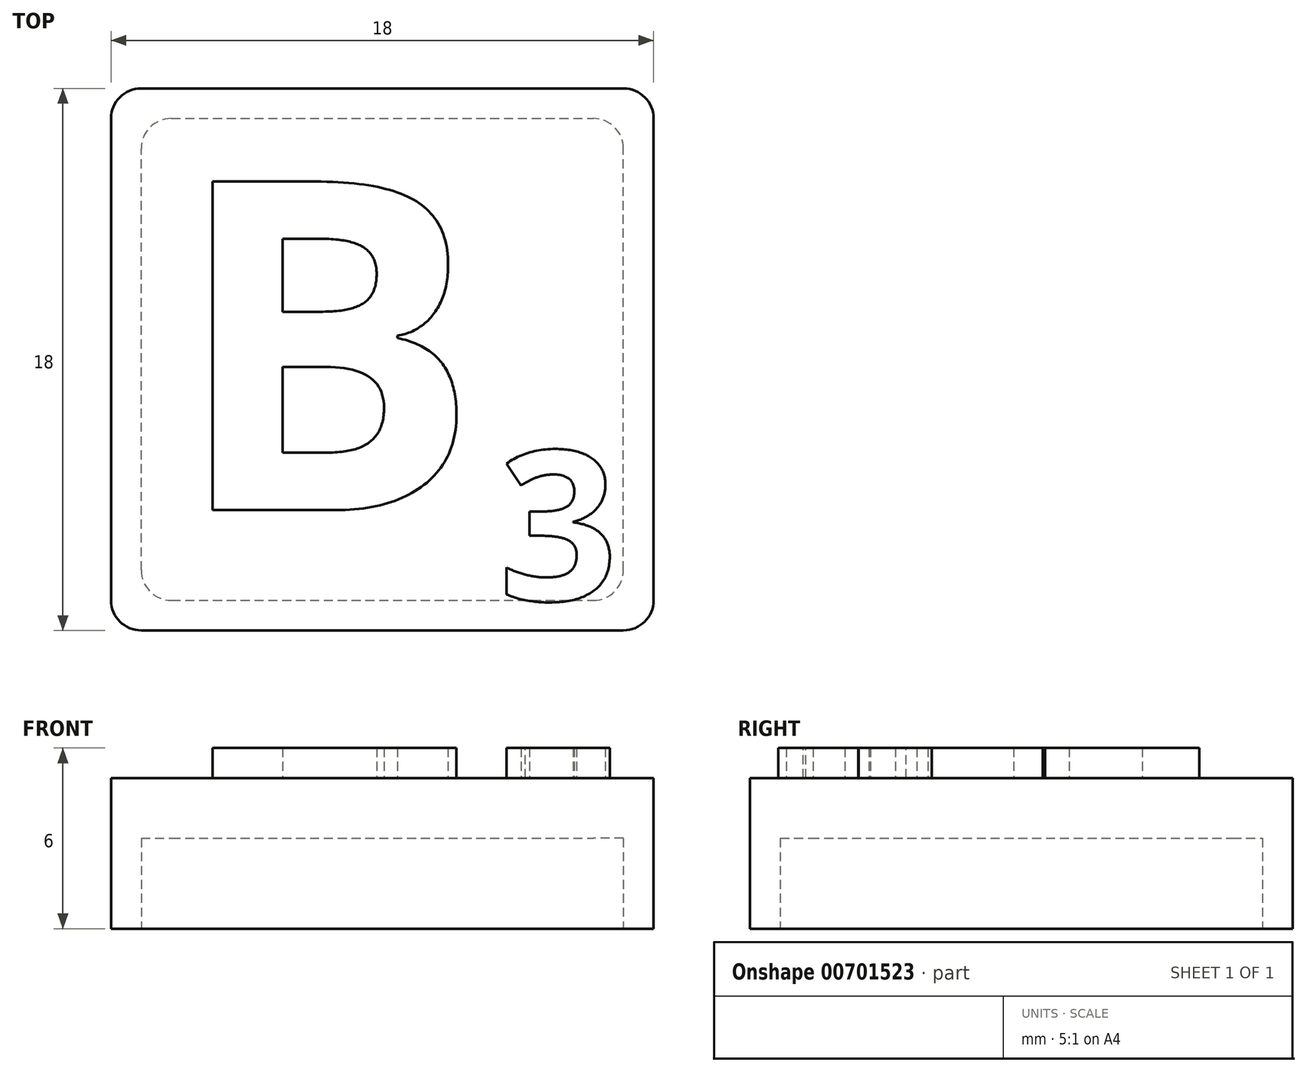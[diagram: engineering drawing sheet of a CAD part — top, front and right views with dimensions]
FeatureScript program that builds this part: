
annotation { "Feature Type Name" : "Feature", "Feature Type Description" : "" }
export const myFeature = defineFeature(function(context is Context, id is Id, definition is map)
    precondition{}
    {
        {
            var Q0;
            Q0=qCreatedBy(makeId("Top.planeOp"),FACE);
            var sketch = newSketch(context, id + "F0", { "sketchPlane" : qUnion([Q0])});
            skLineSegment(sketch, "E0.bottom", {"start": v(-3.93, 7.24) * mm, "end": v(14.07, 7.24) * mm});
            skLineSegment(sketch, "E0.top", {"start": v(-3.93, -10.76) * mm, "end": v(14.07, -10.76) * mm});
            skLineSegment(sketch, "E0.left", {"start": v(-3.93, 7.24) * mm, "end": v(-3.93, -10.76) * mm});
            skLineSegment(sketch, "E0.right", {"start": v(14.07, 7.24) * mm, "end": v(14.07, -10.76) * mm});
            skSolve(sketch);
        }
        {
            var Q0;
            Q0=qSketchRegion(id+"F0",true);
            extrude(context, id + "F1", {"entities" : qUnion([Q0]), "depth" : 5 * mm, "offsetDistance" : 25 * mm});
        }
        {
            var Q0;
            Q0=qCreatedBy(makeId("Top.planeOp"),FACE);
            var sketch = newSketch(context, id + "F2", { "sketchPlane" : qUnion([Q0])});
            skLineSegment(sketch, "E1.bottom", {"start": v(-2.93, -9.76) * mm, "end": v(13.07, -9.76) * mm});
            skLineSegment(sketch, "E1.top", {"start": v(-2.93, 6.24) * mm, "end": v(13.07, 6.24) * mm});
            skLineSegment(sketch, "E1.left", {"start": v(-2.93, -9.76) * mm, "end": v(-2.93, 6.24) * mm});
            skLineSegment(sketch, "E1.right", {"start": v(13.07, -9.76) * mm, "end": v(13.07, 6.24) * mm});
            skSolve(sketch);
        }
        {
            var Q0;
            Q0=makeQuery(id+"F2.imprint","IMPRINT",FACE,{"disambiguationData":[TD([[makeQuery(id+"F2.imprint","IMPRINT",EDGE,{"derivedFrom":sQuery(id+"F2.wireOp",EDGE,"E1.bottom")}),1.0]])]});
            extrude(context, id + "F3", {"entities" : qUnion([Q0]), "operationType" : NewBodyOperationType.REMOVE, "depth" : 3 * mm, "offsetDistance" : 25 * mm});
        }
        {
            var Q0;
            Q0=makeQuery(id+"F1.opExtrude","CAP_FACE",FACE,{"disambiguationData":[OSD([sQuery(id+"F0.wireOp",EDGE,"E0.bottom"),sQuery(id+"F0.wireOp",EDGE,"E0.top"),sQuery(id+"F0.wireOp",EDGE,"E0.left"),sQuery(id+"F0.wireOp",EDGE,"E0.right")])],"isStart":false});
            var sketch = newSketch(context, id + "F4", { "sketchPlane" : qUnion([Q0])});
            skText(sketch, "E2", { "text": "B", "fontName": "OpenSans-Bold.ttf"});
            skText(sketch, "E3", { "text": "3", "fontName": "OpenSans-Bold.ttf"});
            const initialGuessF4  = {"E2": [-0.00193, -0.00676, 1, 0, 0.011], "E3": [0.00892, -0.00976, 1, 0, 0.005]};
            skSetInitialGuess(sketch, initialGuessF4);
            skSolve(sketch);
        }
        {
            var Q0;
            Q0=makeQuery(id+"F4.imprint","IMPRINT",FACE,{"disambiguationData":[TD([[makeQuery(id+"F4.imprint","IMPRINT",EDGE,{"derivedFrom":sQuery(id+"F4.wireOp",EDGE,"E2.sketch_text.stroke-0")}),-1.0]])]});
            var Q1;
            Q1=makeQuery(id+"F4.imprint","IMPRINT",FACE,{"disambiguationData":[TD([[makeQuery(id+"F4.imprint","IMPRINT",EDGE,{"derivedFrom":sQuery(id+"F4.wireOp",EDGE,"E3.sketch_text.stroke-0")}),-1.0]])]});
            extrude(context, id + "F5", {"entities" : qUnion([Q0, Q1]), "operationType" : NewBodyOperationType.ADD, "depth" : 1 * mm, "offsetDistance" : 25 * mm});
        }
        {
            var Q0;
            Q0=makeQuery(id+"F1.opExtrude","SWEPT_EDGE",EDGE,{"disambiguationData":[OSD([sQuery(id+"F0.wireOp",EDGE,"E0.bottom"),sQuery(id+"F0.wireOp",EDGE,"E0.right")])]});
            var Q1;
            Q1=makeQuery(id+"F1.opExtrude","SWEPT_EDGE",EDGE,{"disambiguationData":[OSD([sQuery(id+"F0.wireOp",EDGE,"E0.top"),sQuery(id+"F0.wireOp",EDGE,"E0.right")])]});
            var Q2;
            Q2=makeQuery(id+"F1.opExtrude","SWEPT_EDGE",EDGE,{"disambiguationData":[OSD([sQuery(id+"F0.wireOp",EDGE,"E0.top"),sQuery(id+"F0.wireOp",EDGE,"E0.left")])]});
            var Q3;
            Q3=makeQuery(id+"F1.opExtrude","SWEPT_EDGE",EDGE,{"disambiguationData":[OSD([sQuery(id+"F0.wireOp",EDGE,"E0.bottom"),sQuery(id+"F0.wireOp",EDGE,"E0.left")])]});
            var Q4;
            Q4=makeQuery(id+"F3.boolean.opBoolean","COPY",EDGE,{"derivedFrom":makeQuery(id+"F3.opExtrude","SWEPT_EDGE",EDGE,{"disambiguationData":[OSD([sQuery(id+"F2.wireOp",EDGE,"E1.bottom"),sQuery(id+"F2.wireOp",EDGE,"E1.right")])]})});
            var Q5;
            Q5=makeQuery(id+"F3.boolean.opBoolean","COPY",EDGE,{"derivedFrom":makeQuery(id+"F3.opExtrude","SWEPT_EDGE",EDGE,{"disambiguationData":[OSD([sQuery(id+"F2.wireOp",EDGE,"E1.bottom"),sQuery(id+"F2.wireOp",EDGE,"E1.left")])]})});
            var Q6;
            Q6=makeQuery(id+"F3.boolean.opBoolean","COPY",EDGE,{"derivedFrom":makeQuery(id+"F3.opExtrude","SWEPT_EDGE",EDGE,{"disambiguationData":[OSD([sQuery(id+"F2.wireOp",EDGE,"E1.top"),sQuery(id+"F2.wireOp",EDGE,"E1.left")])]})});
            var Q7;
            Q7=makeQuery(id+"F3.boolean.opBoolean","COPY",EDGE,{"derivedFrom":makeQuery(id+"F3.opExtrude","SWEPT_EDGE",EDGE,{"disambiguationData":[OSD([sQuery(id+"F2.wireOp",EDGE,"E1.top"),sQuery(id+"F2.wireOp",EDGE,"E1.right")])]})});
            fillet(context, id + "F6", {"entities" : qUnion([Q0, Q1, Q2, Q3, Q4, Q5, Q6, Q7]), "radius" : 1 * mm, "tangentPropagation" : true, "allowEdgeOverflow" : false});
        }
    });
